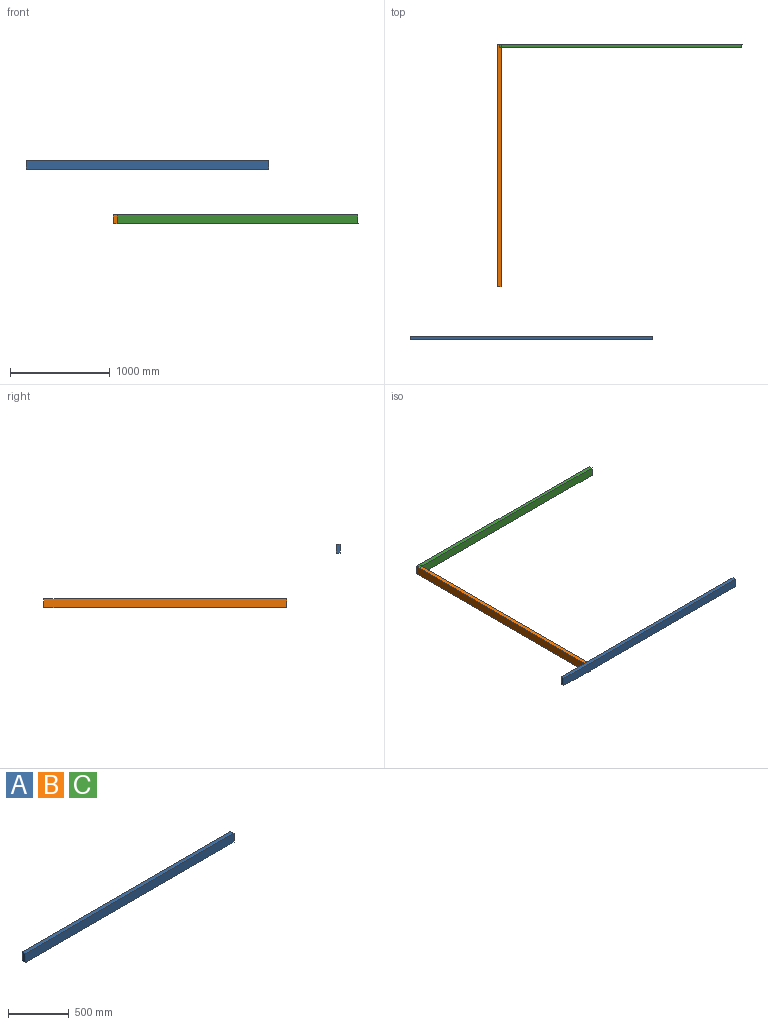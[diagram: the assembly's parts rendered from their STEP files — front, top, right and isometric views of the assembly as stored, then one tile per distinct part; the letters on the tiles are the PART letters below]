
ASSEMBLY  parts=3 mates=1
PART A: 6 faces, bbox 2438.4x38.1x88.9 mm
  f0: plane 88.9x38.1mm, normal (-1,0,0), area 3387.1mm2, adj f1,f3,f4,f5
  f1: plane 2438.4x38.1mm, normal (0,0,-1), area 92903mm2, adj f0,f2,f4,f5
  f2: plane 88.9x38.1mm, normal (1,0,0), area 3387.1mm2, adj f1,f3,f4,f5
  f3: plane 2438.4x38.1mm, normal (0,0,1), area 92903mm2, adj f0,f2,f4,f5
  f4: plane 2438.4x88.9mm, normal (0,-1,0), area 216773.8mm2, adj f0,f1,f2,f3
  f5: plane 2438.4x88.9mm, normal (0,1,0), area 216773.8mm2, adj f0,f1,f2,f3
PART B: same geometry as A
PART C: same geometry as A
PLACE A t=(1449.67,-3303.76,748.8)mm
PLACE B rot(axis=(-0.71,0.71,0),180deg) t=(2058.36,-636.51,275.76)mm
PLACE C t=(2344.87,-369.05,201.41)mm
MATE fastened B.f0 <-> C.f5  axis (0,1,0) through (2077.41,-369.05,238.58)mm
